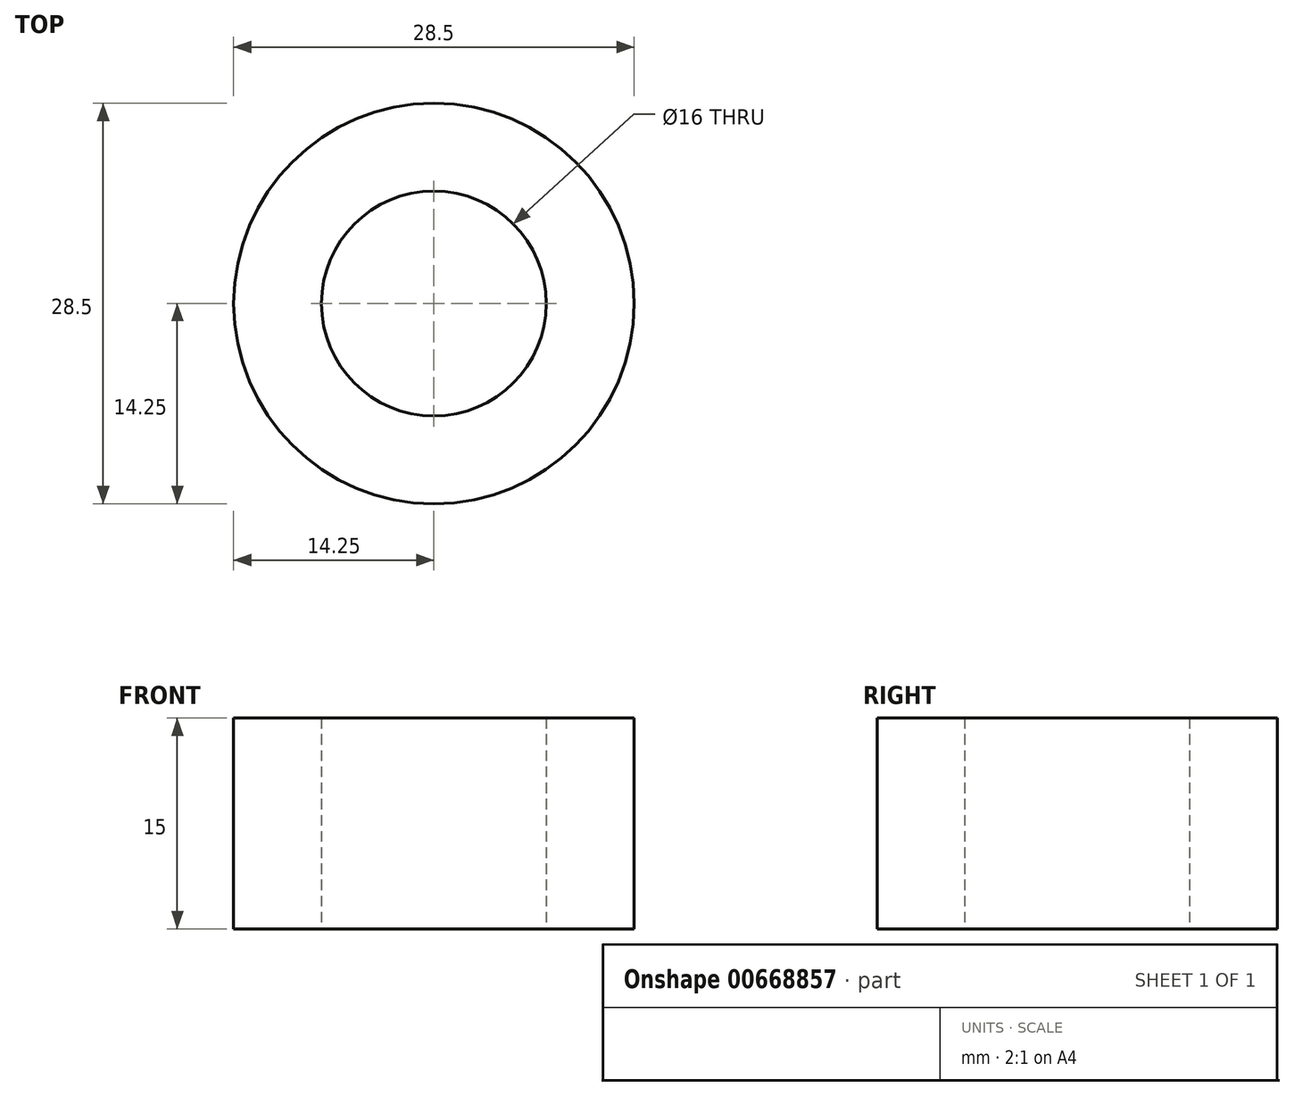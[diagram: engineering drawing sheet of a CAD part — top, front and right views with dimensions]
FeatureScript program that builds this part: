
annotation { "Feature Type Name" : "Feature", "Feature Type Description" : "" }
export const myFeature = defineFeature(function(context is Context, id is Id, definition is map)
    precondition{}
    {
        {
            var Q0;
            Q0=qCreatedBy(makeId("Top.planeOp"),FACE);
            var sketch = newSketch(context, id + "F0", { "sketchPlane" : qUnion([Q0])});
            skCircle(sketch, "E0", {"center": v(0, 0) * mm, "radius": 14.25 * mm});
            skCircle(sketch, "E1", {"center": v(0, 0) * mm, "radius": 8 * mm});
            skSolve(sketch);
        }
        {
            var Q0;
            Q0=makeQuery(id+"F0.imprint","IMPRINT",FACE,{"disambiguationData":[TD([[makeQuery(id+"F0.imprint","IMPRINT",EDGE,{"derivedFrom":sQuery(id+"F0.wireOp",EDGE,"E0")}),1.0]])]});
            extrude(context, id + "F1", {"entities" : qUnion([Q0]), "depth" : 15 * mm, "offsetDistance" : 25 * mm});
        }
    });
